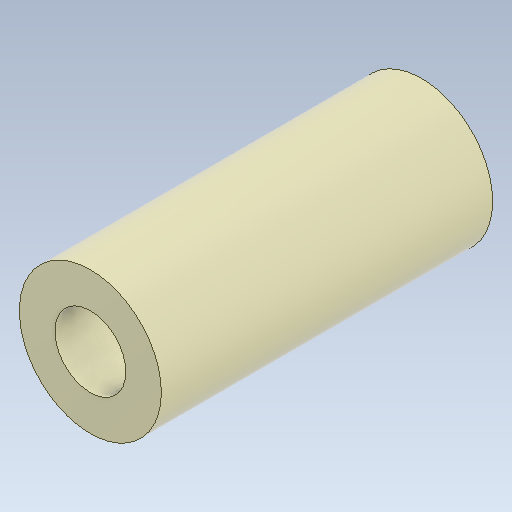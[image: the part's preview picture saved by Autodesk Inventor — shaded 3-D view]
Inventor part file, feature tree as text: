
AUTODESK INVENTOR PART (.ipt)
format: ipt  version: 2020.2 (Build 242310000, 310)  size: 108,544 bytes
history: native  units: mm
features: other x1, extrude x1, sketch x1
ambient origin geometry x8: Origin, YZ Plane, XZ Plane, XY Plane, X Axis, Y Axis, Z Axis, Center Point
bodies: Body1 (feature_tree)
feature tree (3):
  other  "ソリッド1"
  extrude  "押し出し1"  Depth=6.0mm
  sketch  "スケッチ1"
